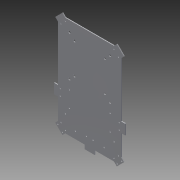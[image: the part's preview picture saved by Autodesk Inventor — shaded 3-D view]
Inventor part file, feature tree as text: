
AUTODESK INVENTOR PART (.ipt)
format: ipt  version: 2013 (Build 170138000, 138)  size: 298,496 bytes
history: native  units: mm
features: sketch x6, hole x4, extrude x2, other x1, projected_geometry x1
ambient origin geometry x8: Origin, YZ Plane, XZ Plane, XY Plane, X Axis, Y Axis, Z Axis, Center Point
feature tree (14):
  other  "ソリッド1"
  extrude  "押し出し1"  Depth=135.0mm
  hole  "穴1"  [1 undecoded]
  hole  "穴2"  [1 undecoded]
  hole  "穴4"  [1 undecoded]
  hole  "穴5"  [1 undecoded]
  extrude  "押し出し2"  Depth=257.0mm
  sketch  "スケッチ1"
  sketch  "スケッチ2"
  sketch  "スケッチ3"
  sketch  "スケッチ5"
  projected_geometry  "投影ループ1"
  sketch  "スケッチ6"
  sketch  "スケッチ7"
note: 4 required parameter values undecoded (feature->parameter linkage not recoverable at this tier; creation-order binding heuristic only, values carry confidence <= 0.55)
